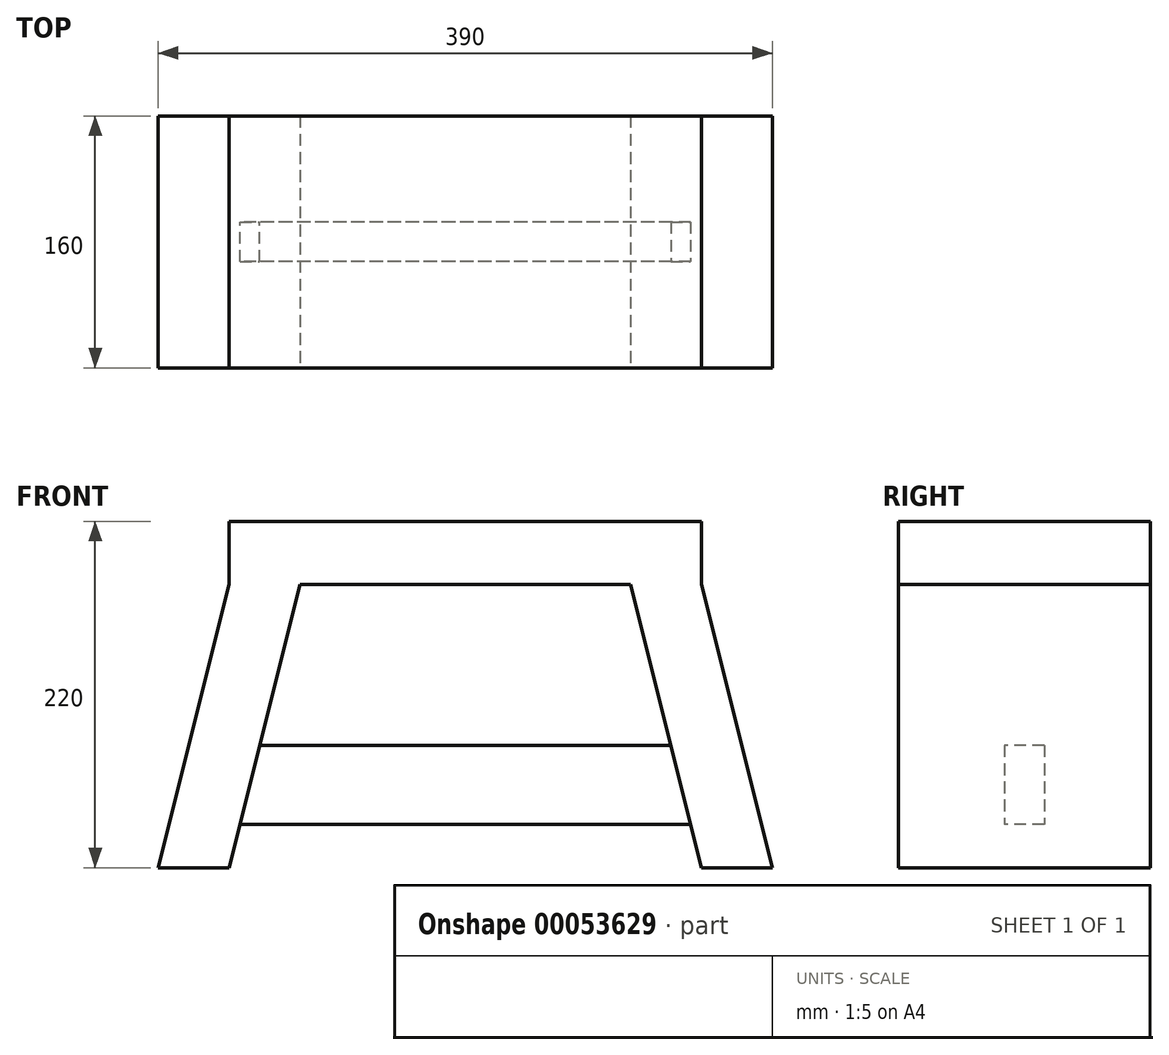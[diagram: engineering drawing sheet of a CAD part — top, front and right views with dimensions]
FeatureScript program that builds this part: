
annotation { "Feature Type Name" : "Feature", "Feature Type Description" : "" }
export const myFeature = defineFeature(function(context is Context, id is Id, definition is map)
    precondition{}
    {
        {
            var Q0;
            Q0=qCreatedBy(makeId("Top.planeOp"),FACE);
            var sketch = newSketch(context, id + "F0", { "sketchPlane" : qUnion([Q0])});
            skLineSegment(sketch, "E0.rect.bottom", {"start": v(150, 80) * mm, "end": v(-150, 80) * mm});
            skLineSegment(sketch, "E0.rect.top", {"start": v(150, -80) * mm, "end": v(-150, -80) * mm});
            skLineSegment(sketch, "E0.rect.left", {"start": v(150, 80) * mm, "end": v(150, -80) * mm});
            skLineSegment(sketch, "E0.rect.right", {"start": v(-150, 80) * mm, "end": v(-150, -80) * mm});
            skPoint(sketch, "E0.rect.middle", {"position": v(0, 0) * mm});
            skSolve(sketch);
        }
        {
            var Q0;
            Q0=makeQuery(id+"F0.imprint","IMPRINT",FACE,{"disambiguationData":[TD([[makeQuery(id+"F0.imprint","IMPRINT",EDGE,{"derivedFrom":sQuery(id+"F0.wireOp",EDGE,"E0.rect.bottom")}),1.0]])]});
            extrude(context, id + "F1", {"entities" : qUnion([Q0]), "depth" : 40 * mm});
        }
        {
            var Q0;
            Q0=makeQuery(id+"F1.opExtrude","CAP_FACE",FACE,{"disambiguationData":[OSD([sQuery(id+"F0.wireOp",EDGE,"E0.rect.bottom"),sQuery(id+"F0.wireOp",EDGE,"E0.rect.top"),sQuery(id+"F0.wireOp",EDGE,"E0.rect.left"),sQuery(id+"F0.wireOp",EDGE,"E0.rect.right")])],"isStart":true});
            cPlane(context, id + "F2", {"entities" : qUnion([Q0]), "cplaneType" : CPlaneType.OFFSET, "offset" : 180 * mm, "width" : 150 * mm, "height" : 150 * mm});
        }
        {
            var Q0;
            Q0=qCreatedBy(id+"F2.planeOp",FACE);
            var sketch = newSketch(context, id + "F3", { "sketchPlane" : qUnion([Q0])});
            skLineSegment(sketch, "E1.0", {"start": v(150, -80) * mm, "end": v(150, 80) * mm});
            skLineSegment(sketch, "E2", {"start": v(150, 80) * mm, "end": v(195, 80) * mm});
            skLineSegment(sketch, "E3", {"start": v(195, 80) * mm, "end": v(195, -80) * mm});
            skLineSegment(sketch, "E4", {"start": v(195, -80) * mm, "end": v(150, -80) * mm});
            skSolve(sketch);
        }
        {
            var Q0;
            Q0=makeQuery(id+"F1.opExtrude","CAP_FACE",FACE,{"disambiguationData":[OSD([sQuery(id+"F0.wireOp",EDGE,"E0.rect.bottom"),sQuery(id+"F0.wireOp",EDGE,"E0.rect.top"),sQuery(id+"F0.wireOp",EDGE,"E0.rect.left"),sQuery(id+"F0.wireOp",EDGE,"E0.rect.right")])],"isStart":true});
            var sketch = newSketch(context, id + "F4", { "sketchPlane" : qUnion([Q0])});
            skLineSegment(sketch, "E5.bottom", {"start": v(150, -80) * mm, "end": v(105, -80) * mm});
            skLineSegment(sketch, "E5.top", {"start": v(150, 80) * mm, "end": v(105, 80) * mm});
            skLineSegment(sketch, "E5.left", {"start": v(150, -80) * mm, "end": v(150, 80) * mm});
            skLineSegment(sketch, "E5.right", {"start": v(105, -80) * mm, "end": v(105, 80) * mm});
            skSolve(sketch);
        }
        {
            var Q1;
            Q1=qSketchRegion(id+"F4",true);
            var Q2;
            Q2=qSketchRegion(id+"F3",true);
            loft(context, id + "F5", {"sheetProfilesArray" : [{ "sheetProfileEntities" : qUnion([Q1]) }, { "sheetProfileEntities" : qUnion([Q2]) }]});
        }
        {
            var Q0;
            Q0=makeQuery(id+"F5.opLoft","SWEPT_BODY",BODY,{"disambiguationData":[OSD([makeQuery(id+"F3.imprint","IMPRINT",FACE,{"disambiguationData":[TD([[makeQuery(id+"F3.imprint","IMPRINT",EDGE,{"derivedFrom":sQuery(id+"F3.wireOp",EDGE,"E1.0")}),-1.0]])]}),makeQuery(id+"F4.imprint","IMPRINT",FACE,{"disambiguationData":[TD([[makeQuery(id+"F4.imprint","IMPRINT",EDGE,{"derivedFrom":sQuery(id+"F4.wireOp",EDGE,"E5.bottom")}),-1.0]])]})])]});
            var Q1;
            Q1=qCreatedBy(makeId("Right.planeOp"),FACE);
            mirror(context, id + "F6", {"operationType" : NewBodyOperationType.ADD, "entities" : qUnion([Q0]), "mirrorPlane" : qUnion([Q1])});
        }
        {
            var Q0;
            Q0=qCreatedBy(makeId("Right.planeOp"),FACE);
            var sketch = newSketch(context, id + "F7", { "sketchPlane" : qUnion([Q0])});
            skLineSegment(sketch, "E6.rect.bottom", {"start": v(12.68, -102.33) * mm, "end": v(-12.68, -102.33) * mm});
            skLineSegment(sketch, "E6.rect.top", {"start": v(12.68, -152.7) * mm, "end": v(-12.68, -152.7) * mm});
            skLineSegment(sketch, "E6.rect.left", {"start": v(12.68, -102.33) * mm, "end": v(12.68, -152.7) * mm});
            skLineSegment(sketch, "E6.rect.right", {"start": v(-12.68, -102.33) * mm, "end": v(-12.68, -152.7) * mm});
            skPoint(sketch, "E6.rect.middle", {"position": v(0, -127.51) * mm});
            skSolve(sketch);
        }
        {
            var Q0;
            Q0 = qSketchRegion(id + "F7", true);
            var Q1;
            Q1=makeQuery(id+"F5.opLoft","SWEPT_FACE",FACE,{"disambiguationData":[OSD([sQuery(id+"F0.wireOp",EDGE,"E0.rect.bottom"),sQuery(id+"F0.wireOp",EDGE,"E0.rect.top"),sQuery(id+"F3.wireOp",EDGE,"E1.0"),sQuery(id+"F3.wireOp",EDGE,"E2"),sQuery(id+"F3.wireOp",EDGE,"E4"),sQuery(id+"F4.wireOp",EDGE,"E5.bottom"),sQuery(id+"F4.wireOp",EDGE,"E5.top"),sQuery(id+"F4.wireOp",EDGE,"E5.right")])]});
            var Q2;
            Q2=makeQuery(id+"F6.opPattern","COPY",FACE,{"derivedFrom":makeQuery(id+"F5.opLoft","SWEPT_FACE",FACE,{"disambiguationData":[OSD([sQuery(id+"F0.wireOp",EDGE,"E0.rect.bottom"),sQuery(id+"F0.wireOp",EDGE,"E0.rect.top"),sQuery(id+"F3.wireOp",EDGE,"E1.0"),sQuery(id+"F3.wireOp",EDGE,"E2"),sQuery(id+"F3.wireOp",EDGE,"E4"),sQuery(id+"F4.wireOp",EDGE,"E5.bottom"),sQuery(id+"F4.wireOp",EDGE,"E5.top"),sQuery(id+"F4.wireOp",EDGE,"E5.right")])]}),"instanceName":"1"});
            extrude(context, id + "F8", {"entities" : qUnion([Q0]), "operationType" : NewBodyOperationType.ADD, "endBound" : BoundingType.UP_TO_SURFACE, "endBoundEntityFace" : qUnion([Q1]), "depth" : 25 * mm, "hasSecondDirection" : true, "secondDirectionBound" : BoundingType.UP_TO_SURFACE, "secondDirectionOppositeDirection" : true, "secondDirectionBoundEntityFace" : qUnion([Q2]), "secondDirectionDepth" : 25 * mm});
        }
    });
